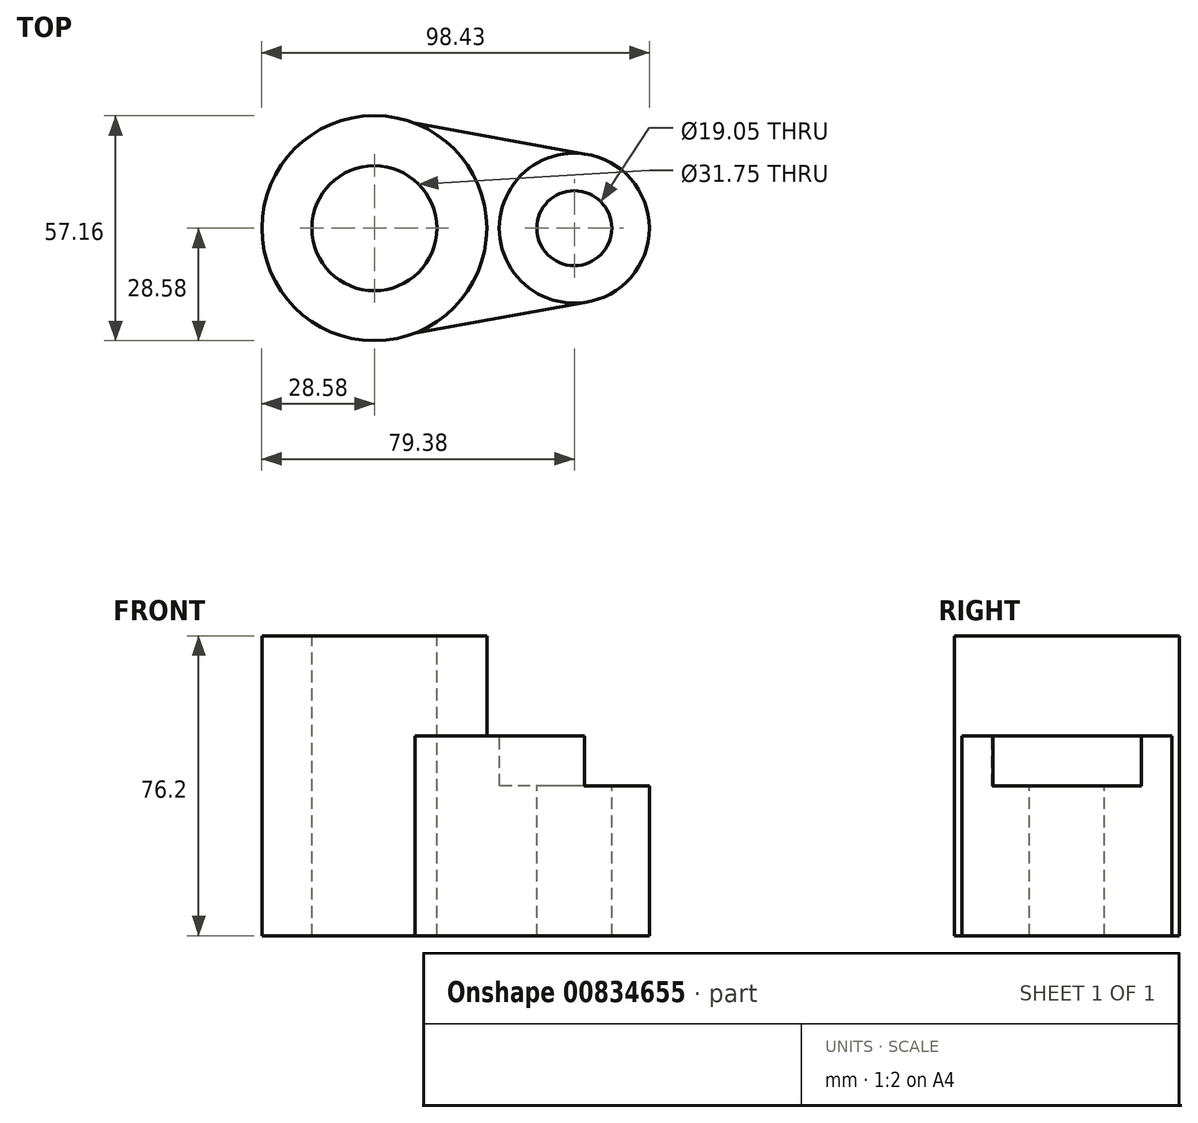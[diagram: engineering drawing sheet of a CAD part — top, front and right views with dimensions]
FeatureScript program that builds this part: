
annotation { "Feature Type Name" : "Feature", "Feature Type Description" : "" }
export const myFeature = defineFeature(function(context is Context, id is Id, definition is map)
    precondition{}
    {
        {
            var Q0;
            Q0=qCreatedBy(makeId("Top.planeOp"),FACE);
            var sketch = newSketch(context, id + "F0", { "sketchPlane" : qUnion([Q0])});
            skCircle(sketch, "E0", {"center": v(0, 0) * mm, "radius": 15.88 * mm});
            skCircle(sketch, "E1", {"center": v(0, 0) * mm, "radius": 28.58 * mm});
            skCircle(sketch, "E2", {"center": v(50.8, 0) * mm, "radius": 9.53 * mm});
            skCircle(sketch, "E3", {"center": v(50.8, 0) * mm, "radius": 19.05 * mm});
            skLineSegment(sketch, "E4", {"start": v(10.32, 26.65) * mm, "end": v(53.34, 18.88) * mm});
            skLineSegment(sketch, "E5", {"start": v(10.32, -26.65) * mm, "end": v(53.34, -18.88) * mm});
            skSolve(sketch);
        }
        {
            var Q0;
            {var subQ0=sQuery(id+"F0.wireOp",EDGE,"E4");var subQ1=sQuery(id+"F0.wireOp",EDGE,"E1");var subQ2=makeQuery(id+"F0.imprint","INTERSECT",VERTEX,{"derivedFrom":[subQ1,subQ0]});Q0=makeQuery(id+"F0.imprint","IMPRINT",FACE,{"disambiguationData":[TD([[makeQuery(id+"F0.imprint","IMPRINT",EDGE,{"disambiguationData":[TD([[subQ2,1.0]])],"derivedFrom":subQ1}),-1.0]])]});}
            var Q1;
            Q1=makeQuery(id+"F0.imprint","IMPRINT",FACE,{"disambiguationData":[TD([[makeQuery(id+"F0.imprint","IMPRINT",EDGE,{"derivedFrom":sQuery(id+"F0.wireOp",EDGE,"E0")}),-1.0]])]});
            var Q2;
            Q2=makeQuery(id+"F0.imprint","IMPRINT",FACE,{"disambiguationData":[TD([[makeQuery(id+"F0.imprint","IMPRINT",EDGE,{"derivedFrom":sQuery(id+"F0.wireOp",EDGE,"E2")}),-1.0]])]});
            extrude(context, id + "F1", {"entities" : qUnion([Q0, Q1, Q2]), "oppositeDirection" : true, "depth" : 76.2 * mm, "offsetDistance" : 25.4 * mm});
        }
        {
            var Q0;
            Q0=makeQuery(id+"F0.imprint","IMPRINT",FACE,{"disambiguationData":[TD([[makeQuery(id+"F0.imprint","IMPRINT",EDGE,{"derivedFrom":sQuery(id+"F0.wireOp",EDGE,"E2")}),-1.0]])]});
            extrude(context, id + "F2", {"entities" : qUnion([Q0]), "operationType" : NewBodyOperationType.REMOVE, "oppositeDirection" : true, "depth" : 38.1 * mm, "offsetDistance" : 25.4 * mm});
        }
        {
            var Q0;
            {var subQ0=sQuery(id+"F0.wireOp",EDGE,"E4");var subQ1=sQuery(id+"F0.wireOp",EDGE,"E1");var subQ2=makeQuery(id+"F0.imprint","INTERSECT",VERTEX,{"derivedFrom":[subQ1,subQ0]});Q0=makeQuery(id+"F0.imprint","IMPRINT",FACE,{"disambiguationData":[TD([[makeQuery(id+"F0.imprint","IMPRINT",EDGE,{"disambiguationData":[TD([[subQ2,1.0]])],"derivedFrom":subQ1}),-1.0]])]});}
            extrude(context, id + "F3", {"entities" : qUnion([Q0]), "operationType" : NewBodyOperationType.REMOVE, "oppositeDirection" : true, "depth" : 25.4 * mm, "offsetDistance" : 25.4 * mm});
        }
        {
            var Q0;
            {var subQ0=sQuery(id+"F0.wireOp",EDGE,"E5");var subQ1=sQuery(id+"F0.wireOp",EDGE,"E3");Q0=makeQuery(id+"F2.boolean.opBoolean","SPLIT",EDGE,{"disambiguationData":[topologyDisambiguationEdgeConnected([makeQuery(id+"F2.opExtrude","SWEPT_FACE",FACE,{"disambiguationData":[OSD([subQ1])]})])],"derivedFrom":makeQuery(id+"F1.opExtrude","SWEPT_EDGE",EDGE,{"disambiguationData":[OSD([subQ1,subQ0])]})});}
            var Q1;
            {var subQ0=sQuery(id+"F0.wireOp",EDGE,"E4");var subQ1=sQuery(id+"F0.wireOp",EDGE,"E3");Q1=makeQuery(id+"F2.boolean.opBoolean","SPLIT",EDGE,{"disambiguationData":[topologyDisambiguationEdgeConnected([makeQuery(id+"F2.opExtrude","SWEPT_FACE",FACE,{"disambiguationData":[OSD([subQ1])]})])],"derivedFrom":makeQuery(id+"F1.opExtrude","SWEPT_EDGE",EDGE,{"disambiguationData":[OSD([subQ1,subQ0])]})});}
            fillet(context, id + "F4", {"entities" : qUnion([Q0, Q1]), "radius" : 5.08 * mm, "tangentPropagation" : true, "allowEdgeOverflow" : false});
        }
    });
